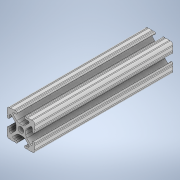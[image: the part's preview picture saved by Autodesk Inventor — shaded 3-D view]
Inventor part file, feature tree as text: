
AUTODESK INVENTOR PART (.ipt)
format: ipt  version: 2020 (Build 240168000, 168)  size: 234,496 bytes
history: native  units: in
note: dims shown in document units (in); Inventor stores cm internally (conversion verified against a paired STEP export)
features: extrude x1, sketch x1
ambient origin geometry x8: Origin, YZ Plane, XZ Plane, XY Plane, X Axis, Y Axis, Z Axis, Center Point
bodies: Solid1 (feature_tree)
feature tree (2):
  extrude  "Extrusion1"  [1 undecoded]
  sketch  "Sketch1"  dims[d0=5.0in d1=0.0in]
note: 1 required parameter value undecoded (feature->parameter linkage not recoverable at this tier; creation-order binding heuristic only, values carry confidence <= 0.55)
